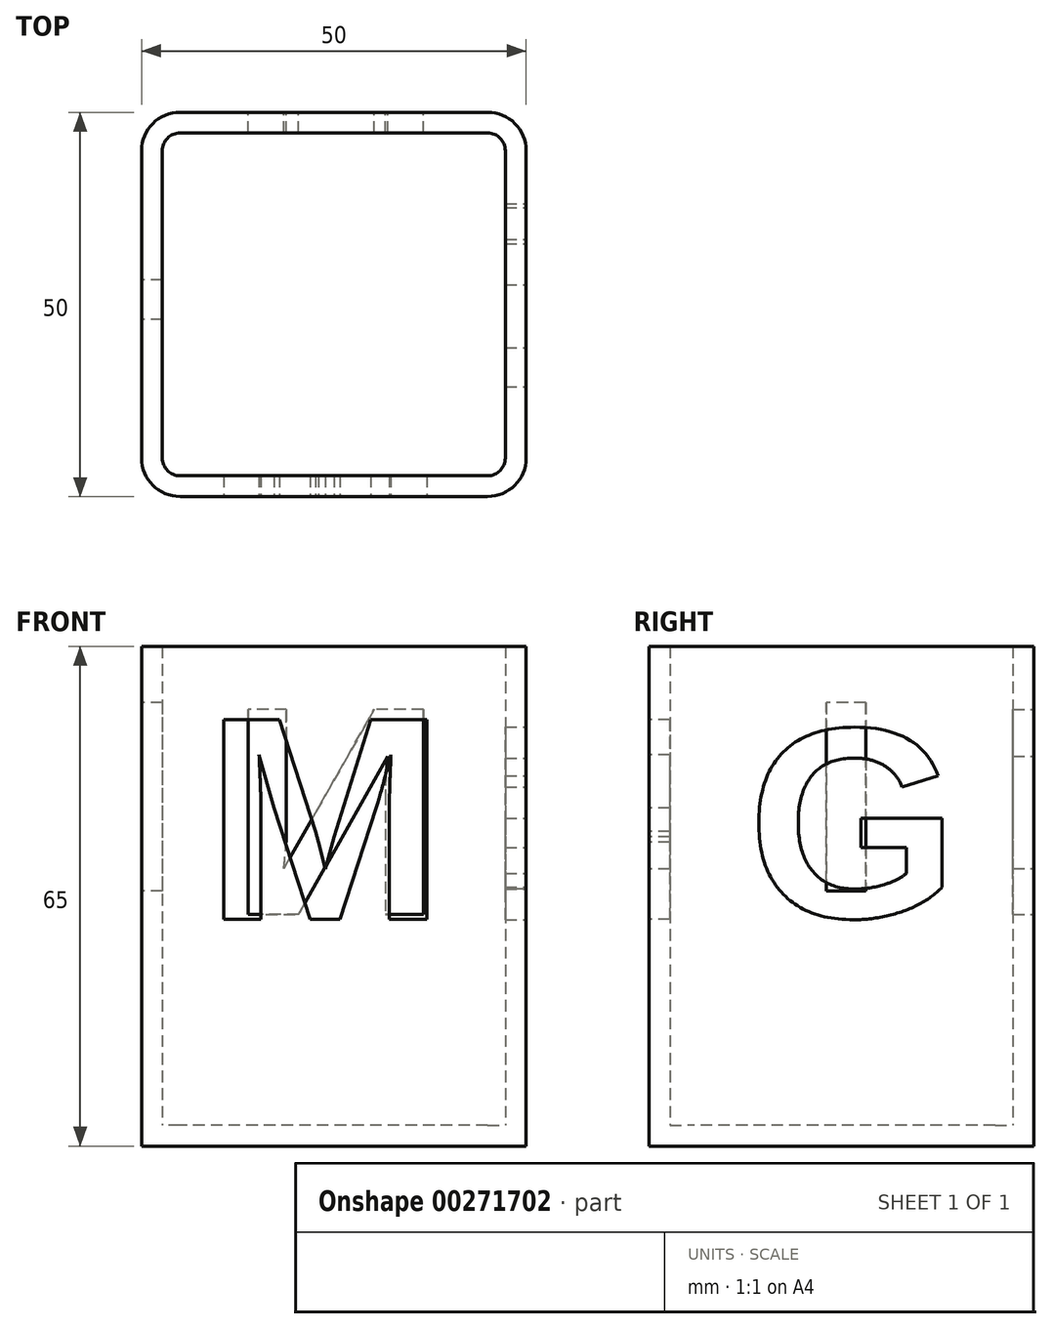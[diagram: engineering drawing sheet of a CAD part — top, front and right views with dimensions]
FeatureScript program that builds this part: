
annotation { "Feature Type Name" : "Feature", "Feature Type Description" : "" }
export const myFeature = defineFeature(function(context is Context, id is Id, definition is map)
    precondition{}
    {
        {
            var Q0;
            Q0=qCreatedBy(makeId("Top.planeOp"),FACE);
            var sketch = newSketch(context, id + "F0", { "sketchPlane" : qUnion([Q0])});
            skLineSegment(sketch, "E0.bottom", {"start": v(20, 25) * mm, "end": v(-20, 25) * mm});
            skLineSegment(sketch, "E0.top", {"start": v(20, -25) * mm, "end": v(-20, -25) * mm});
            skLineSegment(sketch, "E0.left", {"start": v(25, 20) * mm, "end": v(25, -20) * mm});
            skLineSegment(sketch, "E0.right", {"start": v(-25, 20) * mm, "end": v(-25, -20) * mm});
            skPoint(sketch, "E0.middle", {"position": v(0, 0) * mm});
            skPoint(sketch, "E1.visualSharp", {"position": v(-25, -25) * mm});
            skArc(sketch, "E1.filletArc", {"start": v(-25, -20) * mm, "mid": v(-23.54, -23.54) * mm, "end": v(-20, -25) * mm});
            skPoint(sketch, "E2.visualSharp", {"position": v(25, -25) * mm});
            skArc(sketch, "E2.filletArc", {"start": v(20, -25) * mm, "mid": v(23.54, -23.54) * mm, "end": v(25, -20) * mm});
            skPoint(sketch, "E3.visualSharp", {"position": v(25, 25) * mm});
            skArc(sketch, "E3.filletArc", {"start": v(25, 20) * mm, "mid": v(23.54, 23.54) * mm, "end": v(20, 25) * mm});
            skPoint(sketch, "E4.visualSharp", {"position": v(-25, 25) * mm});
            skArc(sketch, "E4.filletArc", {"start": v(-20, 25) * mm, "mid": v(-23.54, 23.54) * mm, "end": v(-25, 20) * mm});
            skSolve(sketch);
        }
        {
            var Q0;
            Q0=makeQuery(id+"F0.imprint","IMPRINT",FACE,{"disambiguationData":[TD([[makeQuery(id+"F0.imprint","IMPRINT",EDGE,{"derivedFrom":sQuery(id+"F0.wireOp",EDGE,"E0.bottom")}),1.0]])]});
            extrude(context, id + "F1", {"entities" : qUnion([Q0]), "depth" : 65 * mm});
        }
        {
            var Q0;
            Q0=makeQuery(id+"F1.opExtrude","CAP_FACE",FACE,{"disambiguationData":[OSD([sQuery(id+"F0.wireOp",EDGE,"E0.bottom"),sQuery(id+"F0.wireOp",EDGE,"E0.top"),sQuery(id+"F0.wireOp",EDGE,"E0.left"),sQuery(id+"F0.wireOp",EDGE,"E0.right")])],"isStart":false});
            shell(context, id + "F2", {"entities" : qUnion([Q0]), "thickness" : 2.7 * mm});
        }
        {
            var Q0;
            Q0=makeQuery(id+"F1.opExtrude","SWEPT_FACE",FACE,{"disambiguationData":[OSD([sQuery(id+"F0.wireOp",EDGE,"E0.right")])]});
            var sketch = newSketch(context, id + "F3", { "sketchPlane" : qUnion([Q0])});
            skText(sketch, "E5", { "text": "I", "fontName": "Arimo-Bold.ttf"});
            const initialGuessF3  = {"E5": [-0.00555, 0.03316, 1, 0, 0.02566]};
            skSetInitialGuess(sketch, initialGuessF3);
            skSolve(sketch);
        }
        {
            var Q0;
            Q0=makeQuery(id+"F1.opExtrude","SWEPT_FACE",FACE,{"disambiguationData":[OSD([sQuery(id+"F0.wireOp",EDGE,"E0.top")])]});
            var sketch = newSketch(context, id + "F4", { "sketchPlane" : qUnion([Q0])});
            skText(sketch, "E6", { "text": "M", "fontName": "Arimo-Bold.ttf"});
            const initialGuessF4  = {"E6": [-0.01687, 0.02949, 1, 0, 0.0272]};
            skSetInitialGuess(sketch, initialGuessF4);
            skSolve(sketch);
        }
        {
            var Q0;
            Q0=makeQuery(id+"F3.imprint","IMPRINT",FACE,{"disambiguationData":[TD([[makeQuery(id+"F3.imprint","IMPRINT",EDGE,{"derivedFrom":sQuery(id+"F3.wireOp",EDGE,"E5.sketch_text.stroke-0")}),-1.0]])]});
            var Q1;
            Q1 = qConstructionFilter(qBodyType(qCreatedBy(id + "F3" ,EDGE), BodyType.WIRE), ConstructionObject.NO);
            extrude(context, id + "F5", {"entities" : qUnion([Q0]), "operationType" : NewBodyOperationType.REMOVE, "surfaceEntities" : qUnion([Q1]), "oppositeDirection" : true, "depth" : 17 * mm});
        }
        {
            var Q0;
            Q0 = qSketchRegion(id + "F4", true);
            extrude(context, id + "F6", {"entities" : qUnion([Q0]), "operationType" : NewBodyOperationType.REMOVE, "oppositeDirection" : true, "depth" : 15.3 * mm});
        }
        {
            var Q0;
            Q0=makeQuery(id+"F1.opExtrude","SWEPT_FACE",FACE,{"disambiguationData":[OSD([sQuery(id+"F0.wireOp",EDGE,"E0.left")])]});
            var sketch = newSketch(context, id + "F7", { "sketchPlane" : qUnion([Q0])});
            skText(sketch, "E7", { "text": "G", "fontName": "Arimo-Bold.ttf"});
            const initialGuessF7  = {"E7": [-0.01219, 0.0298, 1, 0, 0.02546]};
            skSetInitialGuess(sketch, initialGuessF7);
            skSolve(sketch);
        }
        {
            var Q0;
            Q0=makeQuery(id+"F7.imprint","IMPRINT",FACE,{"disambiguationData":[TD([[makeQuery(id+"F7.imprint","IMPRINT",EDGE,{"derivedFrom":sQuery(id+"F7.wireOp",EDGE,"E7.sketch_text.stroke-0")}),-1.0]])]});
            extrude(context, id + "F8", {"entities" : qUnion([Q0]), "operationType" : NewBodyOperationType.REMOVE, "oppositeDirection" : true, "depth" : 12 * mm});
        }
        {
            var Q0;
            Q0=makeQuery(id+"F1.opExtrude","SWEPT_FACE",FACE,{"disambiguationData":[OSD([sQuery(id+"F0.wireOp",EDGE,"E0.bottom")])]});
            var sketch = newSketch(context, id + "F9", { "sketchPlane" : qUnion([Q0])});
            skSolve(sketch);
        }
        {
            var Q0;
            {var subQ0=sQuery(id+"F0.wireOp",EDGE,"E0.bottom");Q0=makeQuery(id+"F9.imprint","IMPRINT",FACE,{"disambiguationData":[TD([[makeQuery(id+"F9.imprint","IMPRINT",EDGE,{"derivedFrom":makeQuery(id+"F1.opExtrude","CAP_EDGE",EDGE,{"disambiguationData":[OSD([subQ0])],"isStart":true})}),1.0]])]});}
            var sketch = newSketch(context, id + "F10", { "sketchPlane" : qUnion([Q0])});
            skText(sketch, "E8", { "text": "N", "fontName": "Arimo-Bold.ttf"});
            const initialGuessF10  = {"E8": [-0.01424, 0.03015, 1, 0, 0.0279]};
            skSetInitialGuess(sketch, initialGuessF10);
            skSolve(sketch);
        }
        {
            var Q0;
            Q0=makeQuery(id+"F10.imprint","IMPRINT",FACE,{"disambiguationData":[TD([[makeQuery(id+"F10.imprint","IMPRINT",EDGE,{"derivedFrom":sQuery(id+"F10.wireOp",EDGE,"E8.sketch_text.stroke-0")}),-1.0]])]});
            extrude(context, id + "F11", {"entities" : qUnion([Q0]), "operationType" : NewBodyOperationType.REMOVE, "oppositeDirection" : true, "depth" : 14 * mm});
        }
    });
